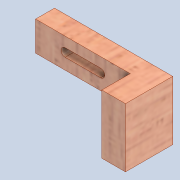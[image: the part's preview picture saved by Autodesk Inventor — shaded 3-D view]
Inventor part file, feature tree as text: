
AUTODESK INVENTOR PART (.ipt)
format: ipt  version: 2020 (Build 240168000, 168)  size: 310,272 bytes
history: native  units: mm
features: extrude x4, sketch x4, fillet x1, mirror x1
ambient origin geometry x8: Origin, YZ Plane, XZ Plane, XY Plane, X Axis, Y Axis, Z Axis, Center Point
bodies: Solid1 (feature_tree)
feature tree (10):
  extrude  "Extrusion1"  Depth=25.0mm
  extrude  "Extrusion5"  Depth=3.5mm
  extrude  "Extrusion6"  Depth=6.0mm
  extrude  "Extrusion7"  Depth=2.0mm
  fillet  "Fillet2"  Radius=15.0mm
  mirror  "Mirror1"
  sketch  "Sketch1"  dims[d0=50.0mm d1=25.0mm]
  sketch  "Sketch5"  dims[d2=20.0mm d3=0.0mm d29=3.5mm]
  sketch  "Sketch6"  dims[d30=4.0mm d31=6.0mm]
  sketch  "Sketch7"  dims[d32=20.0mm d33=15.0mm d34=15.0mm d35=0.0mm d36=10.0mm d37=10.0mm d38=0.0mm d40=12.0mm d41=0.0mm d42=2.0mm]
